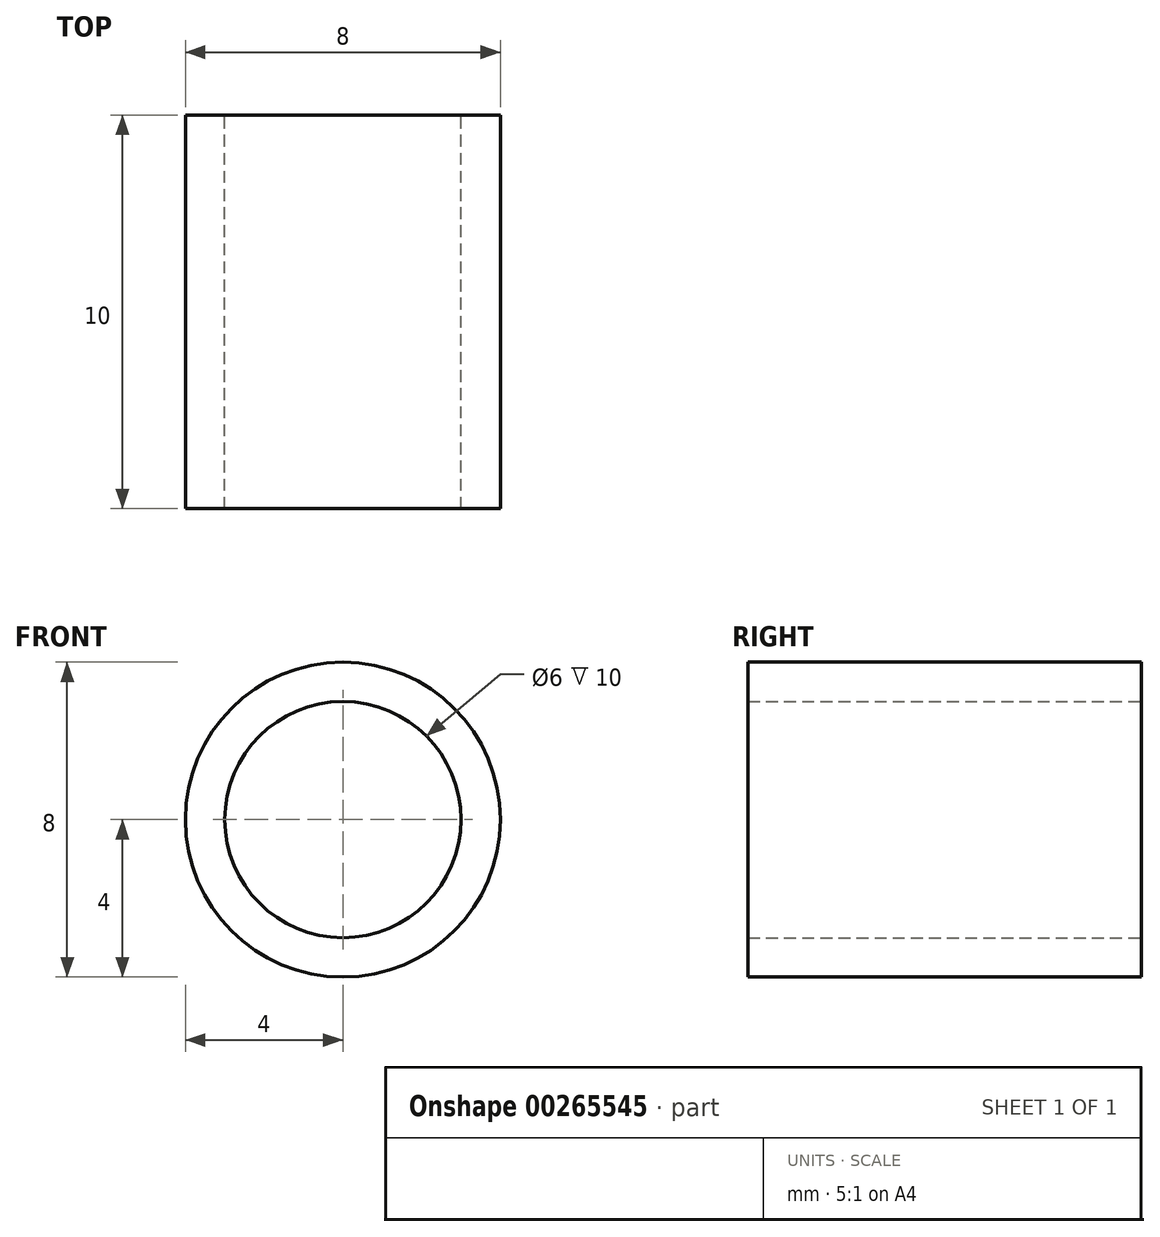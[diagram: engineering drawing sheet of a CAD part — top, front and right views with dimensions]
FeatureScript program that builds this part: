
annotation { "Feature Type Name" : "Feature", "Feature Type Description" : "" }
export const myFeature = defineFeature(function(context is Context, id is Id, definition is map)
    precondition{}
    {
        {
            var Q0;
            Q0=qCreatedBy(makeId("Front.planeOp"),FACE);
            var sketch = newSketch(context, id + "F0", { "sketchPlane" : qUnion([Q0])});
            skCircle(sketch, "E0", {"center": v(0, 0) * mm, "radius": 4 * mm});
            skCircle(sketch, "E1", {"center": v(0, 0) * mm, "radius": 3 * mm});
            skSolve(sketch);
        }
        {
            var Q0;
            Q0=makeQuery(id+"F0.imprint","IMPRINT",FACE,{"disambiguationData":[TD([[makeQuery(id+"F0.imprint","IMPRINT",EDGE,{"derivedFrom":sQuery(id+"F0.wireOp",EDGE,"E0")}),1.0]])]});
            extrude(context, id + "F1", {"entities" : qUnion([Q0]), "depth" : 10 * mm});
        }
    });
